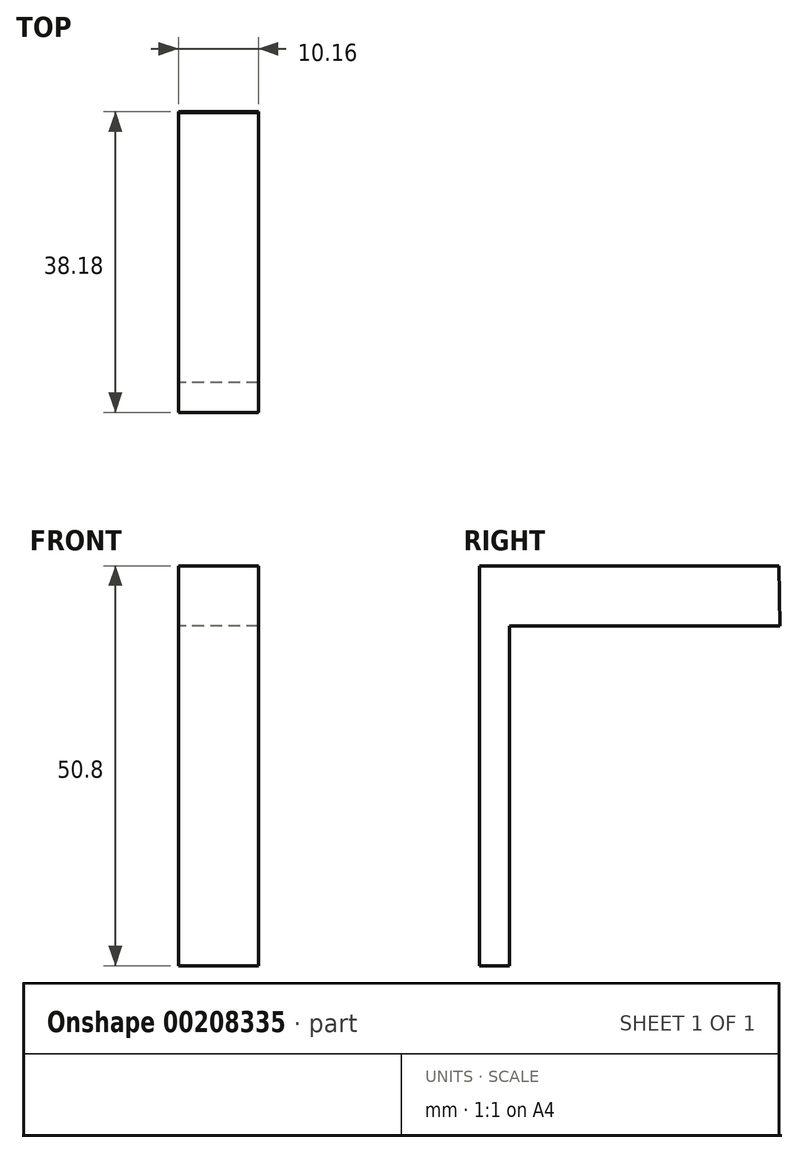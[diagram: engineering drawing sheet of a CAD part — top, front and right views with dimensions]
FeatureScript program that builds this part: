
annotation { "Feature Type Name" : "Feature", "Feature Type Description" : "" }
export const myFeature = defineFeature(function(context is Context, id is Id, definition is map)
    precondition{}
    {
        {
            var Q0;
            Q0=qCreatedBy(makeId("Right.planeOp"),FACE);
            var sketch = newSketch(context, id + "F0", { "sketchPlane" : qUnion([Q0])});
            skLineSegment(sketch, "E0", {"start": v(-5.51, 8.17) * mm, "end": v(-43.61, 8.17) * mm});
            skLineSegment(sketch, "E1", {"start": v(-43.61, 8.17) * mm, "end": v(-43.61, -42.63) * mm});
            skLineSegment(sketch, "E2", {"start": v(-43.61, -42.63) * mm, "end": v(-39.8, -42.63) * mm});
            skLineSegment(sketch, "E3", {"start": v(-39.8, -42.63) * mm, "end": v(-39.8, 0.55) * mm});
            skLineSegment(sketch, "E4", {"start": v(-39.8, 0.55) * mm, "end": v(-5.34, 0.55) * mm});
            skLineSegment(sketch, "E5", {"start": v(-5.51, 8.17) * mm, "end": v(-5.43, 0.55) * mm});
            skPoint(sketch, "E5.endSnap0", {"position": v(-5.43, 1.82) * mm});
            skSolve(sketch);
        }
        {
            var Q0;
            Q0=makeQuery(id+"F0.imprint","IMPRINT",FACE,{"disambiguationData":[TD([[makeQuery(id+"F0.imprint","IMPRINT",EDGE,{"derivedFrom":sQuery(id+"F0.wireOp",EDGE,"E0")}),1.0]])]});
            extrude(context, id + "F1", {"entities" : qUnion([Q0]), "depth" : 10.16 * mm});
        }
    });
